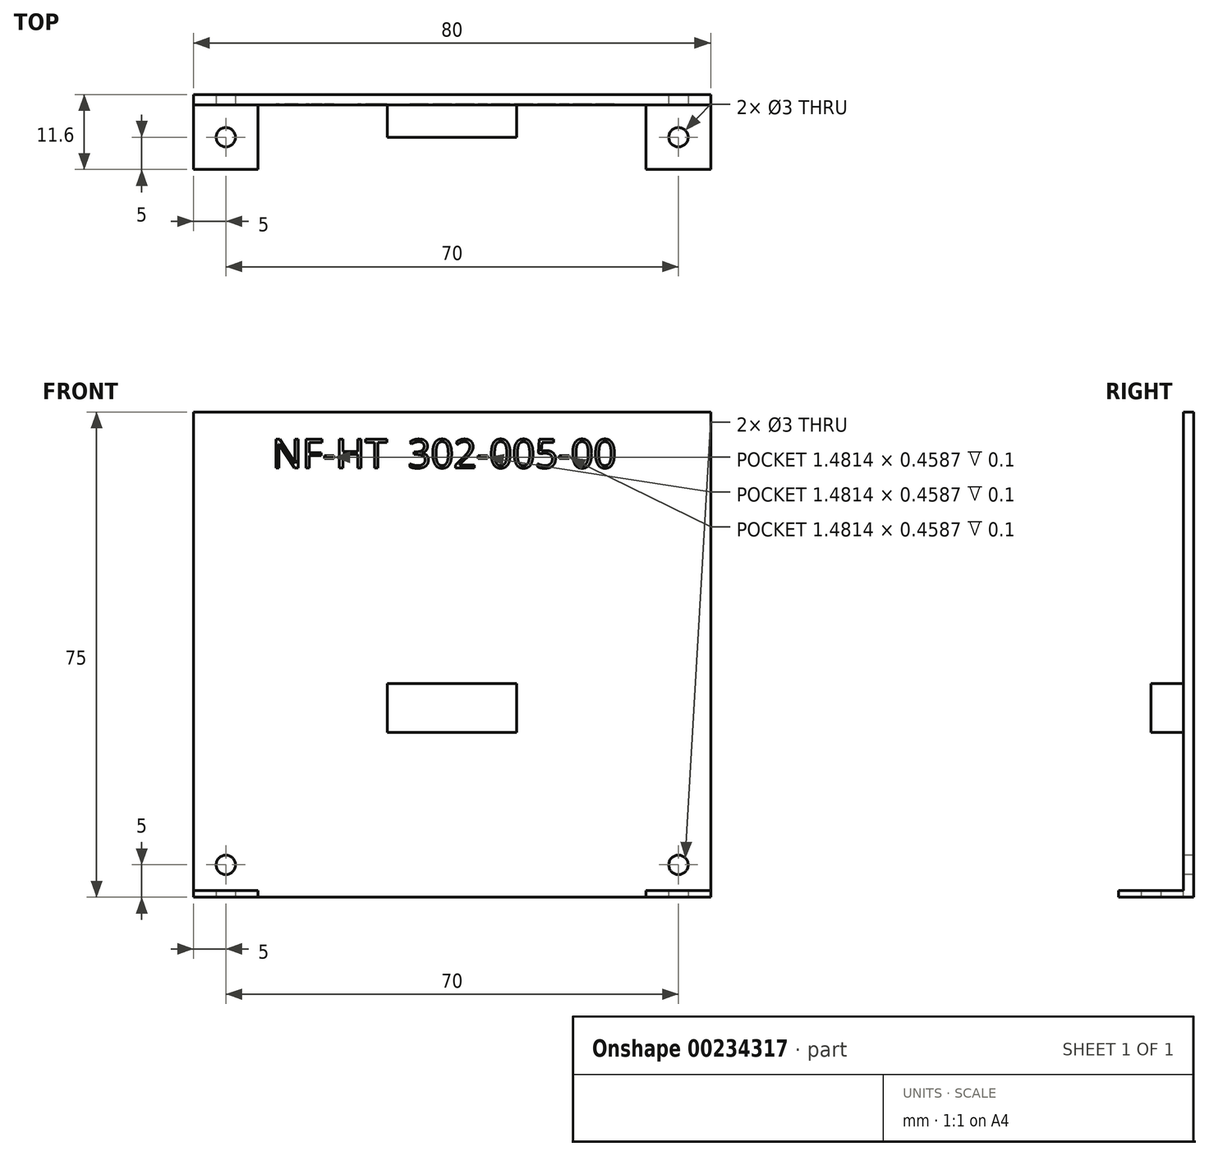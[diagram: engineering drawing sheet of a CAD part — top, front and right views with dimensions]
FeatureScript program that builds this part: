
annotation { "Feature Type Name" : "Feature", "Feature Type Description" : "" }
export const myFeature = defineFeature(function(context is Context, id is Id, definition is map)
    precondition{}
    {
        {
            var Q0;
            Q0=qCreatedBy(makeId("Front.planeOp"),FACE);
            var sketch = newSketch(context, id + "F0", { "sketchPlane" : qUnion([Q0])});
            skLineSegment(sketch, "E0.bottom", {"start": v(40, -37.5) * mm, "end": v(-40, -37.5) * mm});
            skLineSegment(sketch, "E0.top", {"start": v(40, 37.5) * mm, "end": v(-40, 37.5) * mm});
            skLineSegment(sketch, "E0.left", {"start": v(40, -37.5) * mm, "end": v(40, 37.5) * mm});
            skLineSegment(sketch, "E0.right", {"start": v(-40, -37.5) * mm, "end": v(-40, 37.5) * mm});
            skPoint(sketch, "E0.middle", {"position": v(0, 0) * mm});
            skLineSegment(sketch, "E1.bottom", {"start": v(10, -12) * mm, "end": v(-10, -12) * mm});
            skLineSegment(sketch, "E1.top", {"start": v(10, -4.5) * mm, "end": v(-10, -4.5) * mm});
            skLineSegment(sketch, "E1.left", {"start": v(10, -12) * mm, "end": v(10, -4.5) * mm});
            skLineSegment(sketch, "E1.right", {"start": v(-10, -12) * mm, "end": v(-10, -4.5) * mm});
            skPoint(sketch, "E1.middle", {"position": v(0, -8.25) * mm});
            skCircle(sketch, "E2.MirrorC", {"center": v(-35, -32.5) * mm, "radius": 1.5 * mm});
            skCircle(sketch, "E3.MirrorC", {"center": v(35, -32.5) * mm, "radius": 1.5 * mm});
            skLineSegment(sketch, "E4", {"start": v(-30, -37.5) * mm, "end": v(-30, -36.5) * mm});
            skLineSegment(sketch, "E5", {"start": v(-30, -36.5) * mm, "end": v(-40, -36.5) * mm});
            skLineSegment(sketch, "E6.MirrorCS", {"start": v(30, -36.5) * mm, "end": v(40, -36.5) * mm});
            skLineSegment(sketch, "E7.MirrorCS", {"start": v(30, -37.5) * mm, "end": v(30, -36.5) * mm});
            skSolve(sketch);
        }
        {
            var Q0;
            Q0=makeQuery(id+"F0.imprint","IMPRINT",FACE,{"disambiguationData":[TD([[makeQuery(id+"F0.imprint","IMPRINT",EDGE,{"derivedFrom":sQuery(id+"F0.wireOp",EDGE,"E0.bottom")}),-1.0]])]});
            var Q1;
            Q1=makeQuery(id+"F0.imprint","IMPRINT",FACE,{"disambiguationData":[TD([[makeQuery(id+"F0.imprint","IMPRINT",EDGE,{"derivedFrom":sQuery(id+"F0.wireOp",EDGE,"E1.bottom")}),-1.0]])]});
            var Q2;
            {var subQ3=sQuery(id+"F0.wireOp",EDGE,"E0.top");Q2=makeQuery(id+"F0.imprint","IMPRINT",FACE,{"disambiguationData":[TD([[makeQuery(id+"F0.imprint","IMPRINT",EDGE,{"derivedFrom":subQ3}),1.0]])]});}
            extrude(context, id + "F1", {"entities" : qUnion([Q0, Q1, Q2]), "oppositeDirection" : true, "depth" : 1.6 * mm});
        }
        {
            var Q0;
            Q0=makeQuery(id+"F0.imprint","IMPRINT",FACE,{"disambiguationData":[TD([[makeQuery(id+"F0.imprint","IMPRINT",EDGE,{"derivedFrom":sQuery(id+"F0.wireOp",EDGE,"E1.bottom")}),-1.0]])]});
            extrude(context, id + "F2", {"entities" : qUnion([Q0]), "operationType" : NewBodyOperationType.ADD, "depth" : 5 * mm});
        }
        {
            var Q0;
            Q0=makeQuery(id+"F0.imprint","IMPRINT",FACE,{"disambiguationData":[TD([[makeQuery(id+"F0.imprint","IMPRINT",EDGE,{"derivedFrom":sQuery(id+"F0.wireOp",EDGE,"E0.bottom")}),-1.0]])]});
            var sketch = newSketch(context, id + "F3", { "sketchPlane" : qUnion([Q0])});
            skText(sketch, "E8", { "text": "NF-HT  302-005-00", "fontName": "OpenSans-Regular.ttf"});
            const initialGuessF3  = {"E8": [-0.02787, 0.02887, 1, 0, 0.00445]};
            skSetInitialGuess(sketch, initialGuessF3);
            skSolve(sketch);
        }
        {
            var Q0;
            Q0=qSketchRegion(id+"F3",true);
            extrude(context, id + "F4", {"entities" : qUnion([Q0]), "operationType" : NewBodyOperationType.REMOVE, "oppositeDirection" : true, "depth" : .1 * mm});
        }
        {
            var Q0;
            {var subQ3=sQuery(id+"F0.wireOp",EDGE,"E4");Q0=makeQuery(id+"F0.imprint","IMPRINT",FACE,{"disambiguationData":[TD([[makeQuery(id+"F0.imprint","IMPRINT",EDGE,{"derivedFrom":subQ3}),1.0]])]});}
            var Q1;
            {var subQ4=sQuery(id+"F0.wireOp",EDGE,"E6.MirrorCS");Q1=makeQuery(id+"F0.imprint","IMPRINT",FACE,{"disambiguationData":[TD([[makeQuery(id+"F0.imprint","IMPRINT",EDGE,{"derivedFrom":subQ4}),-1.0]])]});}
            extrude(context, id + "F5", {"entities" : qUnion([Q0, Q1]), "operationType" : NewBodyOperationType.ADD, "depth" : 10 * mm});
        }
        {
            var Q0;
            {var subQ0=sQuery(id+"F0.wireOp",EDGE,"E0.bottom");Q0=makeQuery(id+"F5.boolean.opBoolean","MERGE",FACE,{"derivedFrom":[makeQuery(id+"F1.opExtrude","SWEPT_FACE",FACE,{"disambiguationData":[OSD([subQ0])]}),makeQuery(id+"F5.opExtrude","SWEPT_FACE",FACE,{"disambiguationData":[OSD([subQ0]),TDD([makeQuery(id+"F0.imprint","IMPRINT",EDGE,{"disambiguationData":[TD([[makeQuery(id+"F0.imprint","INTERSECT",VERTEX,{"derivedFrom":[subQ0,sQuery(id+"F0.wireOp",EDGE,"E0.left")]}),-1.0]])],"derivedFrom":subQ0})])]}),makeQuery(id+"F5.opExtrude","SWEPT_FACE",FACE,{"disambiguationData":[OSD([subQ0]),TDD([makeQuery(id+"F0.imprint","IMPRINT",EDGE,{"disambiguationData":[TD([[makeQuery(id+"F0.imprint","INTERSECT",VERTEX,{"derivedFrom":[subQ0,sQuery(id+"F0.wireOp",EDGE,"E0.right")]}),1.0]])],"derivedFrom":subQ0})])]})]});}
            var sketch = newSketch(context, id + "F6", { "sketchPlane" : qUnion([Q0])});
            skCircle(sketch, "E9", {"center": v(-35, 5) * mm, "radius": 1.5 * mm});
            skPoint(sketch, "E9.centerSnap0", {"position": v(-35, 10) * mm});
            skCircle(sketch, "E10", {"center": v(35, 5) * mm, "radius": 1.5 * mm});
            skPoint(sketch, "E10.centerSnap0", {"position": v(35, 10) * mm});
            skSolve(sketch);
        }
        {
            var Q0;
            Q0=makeQuery(id+"F6.imprint","IMPRINT",FACE,{"disambiguationData":[TD([[makeQuery(id+"F6.imprint","IMPRINT",EDGE,{"derivedFrom":sQuery(id+"F6.wireOp",EDGE,"E9")}),1.0]])]});
            var Q1;
            Q1=makeQuery(id+"F6.imprint","IMPRINT",FACE,{"disambiguationData":[TD([[makeQuery(id+"F6.imprint","IMPRINT",EDGE,{"derivedFrom":sQuery(id+"F6.wireOp",EDGE,"E10")}),1.0]])]});
            extrude(context, id + "F7", {"entities" : qUnion([Q0, Q1]), "operationType" : NewBodyOperationType.REMOVE, "endBound" : BoundingType.UP_TO_NEXT, "oppositeDirection" : true, "depth" : 25 * mm});
        }
    });
